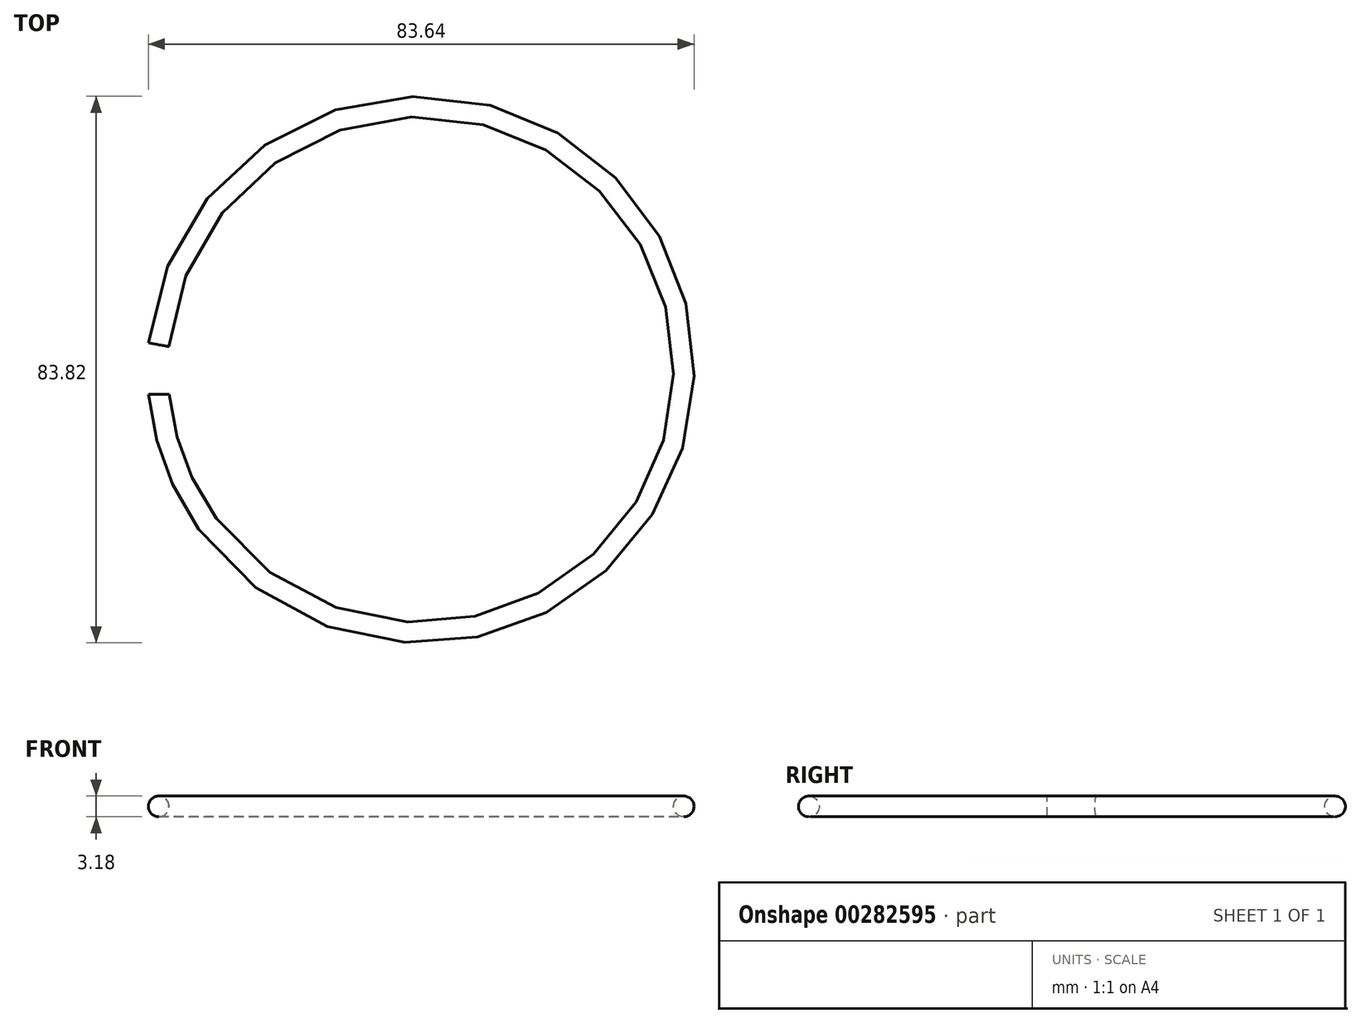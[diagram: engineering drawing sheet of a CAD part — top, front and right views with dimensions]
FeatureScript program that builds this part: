
annotation { "Feature Type Name" : "Feature", "Feature Type Description" : "" }
export const myFeature = defineFeature(function(context is Context, id is Id, definition is map)
    precondition{}
    {
        {
            var Q0;
            Q0=qCreatedBy(makeId("Front.planeOp"),FACE);
            var sketch = newSketch(context, id + "F0", { "sketchPlane" : qUnion([Q0])});
            skCircle(sketch, "E0", {"center": v(0, 0) * mm, "radius": 1.59 * mm});
            skSolve(sketch);
        }
        {
            var Q0;
            Q0=qCreatedBy(makeId("Top.planeOp"),FACE);
            var sketch = newSketch(context, id + "F1", { "sketchPlane" : qUnion([Q0])});
            skArc(sketch, "E1", {"start": v(0, 0) * mm, "mid": v(80.47, 3.81) * mm, "end": v(0, 7.62) * mm});
            skSolve(sketch);
        }
        {
            var Q0;
            Q0=makeQuery(id+"F0.imprint","IMPRINT",FACE,{"disambiguationData":[TD([[makeQuery(id+"F0.imprint","IMPRINT",EDGE,{"derivedFrom":sQuery(id+"F0.wireOp",EDGE,"E0")}),1.0]])]});
            var Q1;
            Q1=sQuery(id+"F1.wireOp",EDGE,"E1");
            sweep(context, id + "F2", {"profiles" : qUnion([Q0]), "path" : qUnion([Q1])});
        }
    });
